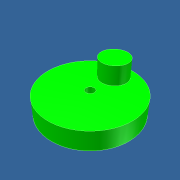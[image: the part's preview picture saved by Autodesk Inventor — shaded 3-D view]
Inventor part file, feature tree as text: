
AUTODESK INVENTOR PART (.ipt)
format: ipt  version: unknown  size: 170,496 bytes
history: native  units: mm
features: extrude x2, sketch x2
ambient origin geometry x8: Origin, YZ Plane, XZ Plane, XY Plane, X Axis, Y Axis, Z Axis, Center Point
feature tree (4):
  extrude  "Выдавливание1"  Depth=1.0mm
  extrude  "Выдавливание2"  Depth=10.0mm
  sketch  "Эскиз1"
  sketch  "Эскиз2"
